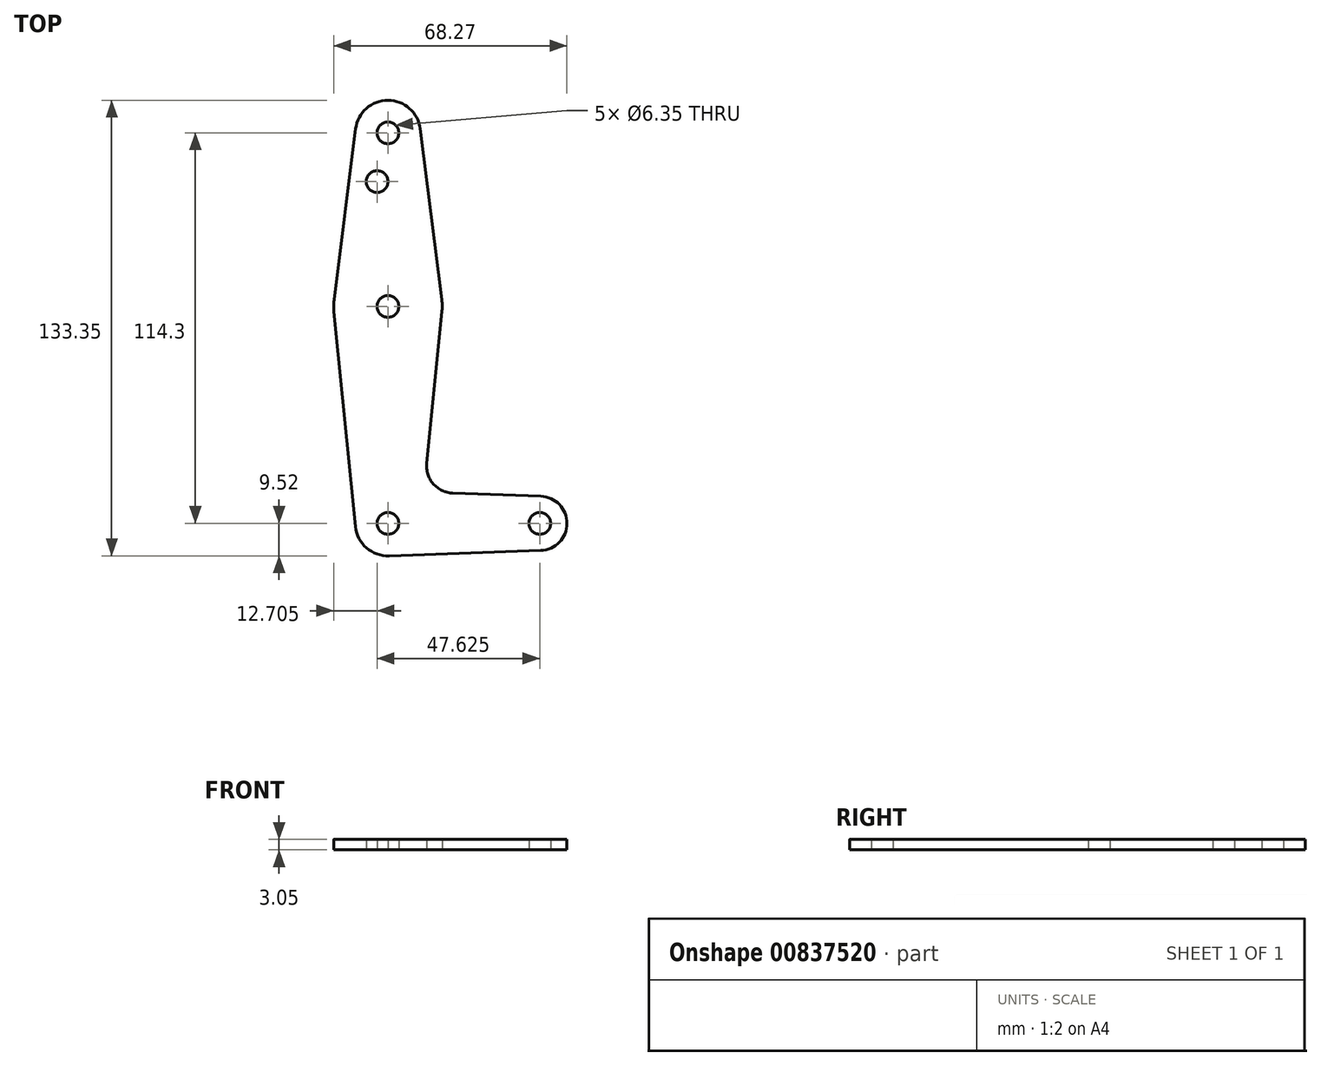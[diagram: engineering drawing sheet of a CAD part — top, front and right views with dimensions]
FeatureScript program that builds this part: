
annotation { "Feature Type Name" : "Feature", "Feature Type Description" : "" }
export const myFeature = defineFeature(function(context is Context, id is Id, definition is map)
    precondition{}
    {
        {
            var Q0;
            Q0=qCreatedBy(makeId("Top.planeOp"),FACE);
            var sketch = newSketch(context, id + "F0", { "sketchPlane" : qUnion([Q0])});
            skLineSegment(sketch, "E0", {"start": v(0, 114.3) * mm, "end": v(0, 0) * mm, "construction": true});
            skLineSegment(sketch, "E1", {"start": v(0, 0) * mm, "end": v(44.45, 0) * mm, "construction": true});
            skCircle(sketch, "E2", {"center": v(0, 114.3) * mm, "radius": 9.52 * mm});
            skCircle(sketch, "E3", {"center": v(0, 63.5) * mm, "radius": 15.88 * mm});
            skCircle(sketch, "E4", {"center": v(0, 0) * mm, "radius": 9.53 * mm});
            skCircle(sketch, "E5", {"center": v(44.45, 0) * mm, "radius": 7.94 * mm});
            skLineSegment(sketch, "E6", {"start": v(-9.45, 115.5) * mm, "end": v(-15.75, 65.48) * mm});
            skLineSegment(sketch, "E7", {"start": v(9.45, 115.5) * mm, "end": v(15.75, 65.48) * mm});
            skLineSegment(sketch, "E8", {"start": v(15.8, 61.91) * mm, "end": v(11.34, 17.6) * mm});
            skLineSegment(sketch, "E9", {"start": v(18.97, 8.85) * mm, "end": v(44.73, 7.93) * mm});
            skLineSegment(sketch, "E10", {"start": v(0.34, -9.52) * mm, "end": v(44.73, -7.93) * mm});
            skCircle(sketch, "E11", {"center": v(0, 114.3) * mm, "radius": 3.18 * mm});
            skCircle(sketch, "E12", {"center": v(0, 63.5) * mm, "radius": 3.18 * mm});
            skCircle(sketch, "E13", {"center": v(0, 0) * mm, "radius": 3.18 * mm});
            skCircle(sketch, "E14", {"center": v(44.45, 0) * mm, "radius": 3.18 * mm});
            skCircle(sketch, "E15", {"center": v(-3.17, 100.03) * mm, "radius": 3.18 * mm});
            skLineSegment(sketch, "E16", {"start": v(-15.8, 61.91) * mm, "end": v(-9.48, -0.95) * mm});
            skLineSegment(sketch, "E17.trimOffspring", {"start": v(9.57, 0) * mm, "end": v(9.48, -0.95) * mm});
            skPoint(sketch, "E18.visualSharp", {"position": v(10.5, 9.16) * mm});
            skArc(sketch, "E18.filletArc", {"start": v(11.34, 17.6) * mm, "mid": v(13.26, 11.57) * mm, "end": v(18.97, 8.85) * mm});
            skSolve(sketch);
        }
        {
            var Q0;
            Q0 = qSketchRegion(id + "F0", true);
            extrude(context, id + "F1", {"entities" : qUnion([Q0]), "depth" : 3.05 * mm, "offsetDistance" : 25.4 * mm});
        }
    });
